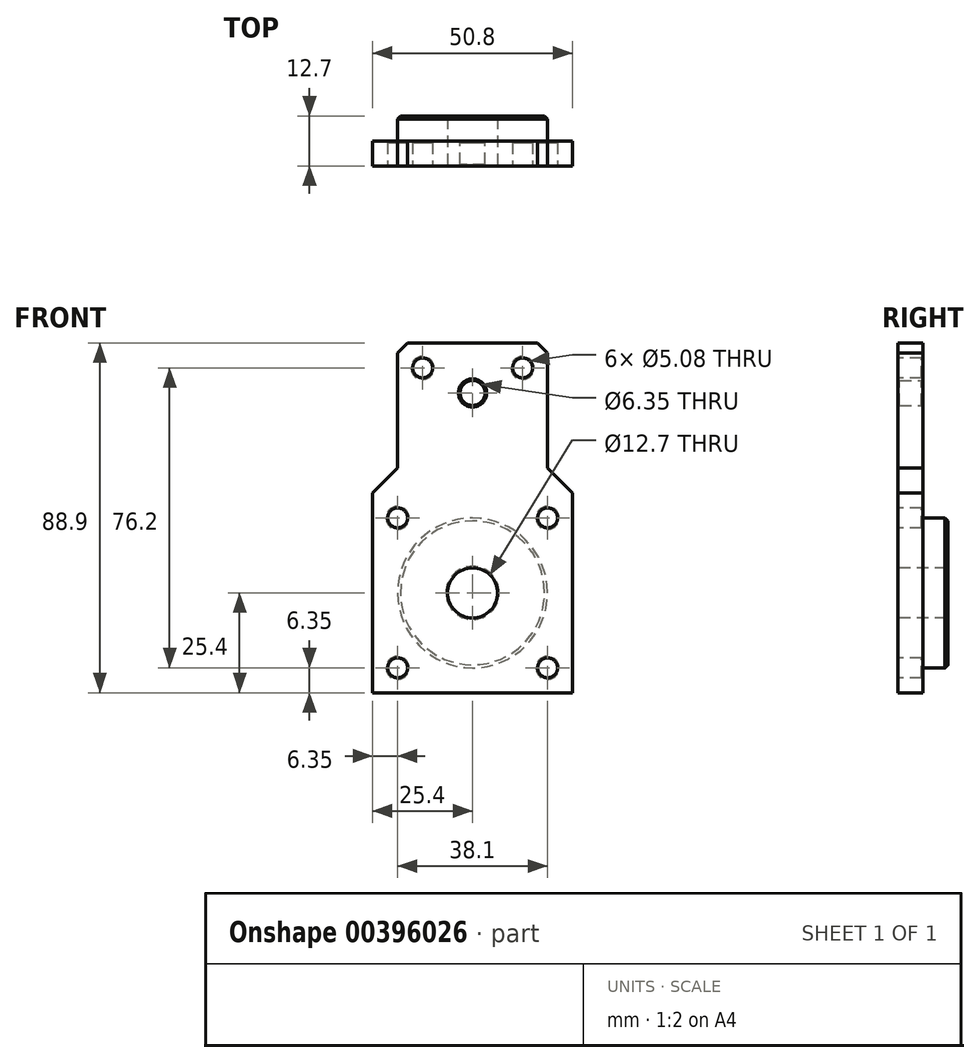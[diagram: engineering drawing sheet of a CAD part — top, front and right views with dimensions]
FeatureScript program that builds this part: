
annotation { "Feature Type Name" : "Feature", "Feature Type Description" : "" }
export const myFeature = defineFeature(function(context is Context, id is Id, definition is map)
    precondition{}
    {
        {
            var Q0;
            Q0=qCreatedBy(makeId("Front.planeOp"),FACE);
            var sketch = newSketch(context, id + "F0", { "sketchPlane" : qUnion([Q0])});
            skCircle(sketch, "E0", {"center": v(0, 0) * mm, "radius": 19.05 * mm});
            skSolve(sketch);
        }
        {
            var Q0;
            Q0 = qSketchRegion(id + "F0", true);
            extrude(context, id + "F1", {"entities" : qUnion([Q0]), "depth" : 6.35 * mm, "offsetDistance" : 25.4 * mm});
        }
        {
            var Q0;
            Q0=makeQuery(id+"F1.opExtrude","CAP_FACE",FACE,{"disambiguationData":[OSD([sQuery(id+"F0.wireOp",EDGE,"E0")])],"isStart":false});
            var sketch = newSketch(context, id + "F2", { "sketchPlane" : qUnion([Q0])});
            skLineSegment(sketch, "E1.bottom", {"start": v(-25.4, 25.4) * mm, "end": v(-19.05, 25.4) * mm});
            skLineSegment(sketch, "E1.top", {"start": v(-25.4, -25.4) * mm, "end": v(25.4, -25.4) * mm});
            skLineSegment(sketch, "E1.left", {"start": v(-25.4, 25.4) * mm, "end": v(-25.4, -25.4) * mm});
            skLineSegment(sketch, "E1.right", {"start": v(25.4, 25.4) * mm, "end": v(25.4, -25.4) * mm});
            skLineSegment(sketch, "E2", {"start": v(-19.05, 63.5) * mm, "end": v(19.05, 63.5) * mm});
            skLineSegment(sketch, "E3", {"start": v(-19.05, 63.5) * mm, "end": v(-19.05, 25.4) * mm});
            skLineSegment(sketch, "E4", {"start": v(19.05, 63.5) * mm, "end": v(19.05, 25.4) * mm});
            skLineSegment(sketch, "E5.trimOffspring", {"start": v(19.05, 25.4) * mm, "end": v(25.4, 25.4) * mm});
            skCircle(sketch, "E6", {"center": v(0, 50.8) * mm, "radius": 3.18 * mm});
            skSolve(sketch);
        }
        {
            var Q0;
            Q0 = qSketchRegion(id + "F2", true);
            extrude(context, id + "F3", {"entities" : qUnion([Q0]), "operationType" : NewBodyOperationType.ADD, "depth" : 6.35 * mm, "offsetDistance" : 25.4 * mm});
        }
        {
            var Q0;
            Q0=makeQuery(id+"F1.opExtrude","CAP_EDGE",EDGE,{"disambiguationData":[OSD([sQuery(id+"F0.wireOp",EDGE,"E0")])],"isStart":true});
            chamfer(context, id + "F4", {"entities" : qUnion([Q0]), "width" : 0.76 * mm, "tangentPropagation" : true});
        }
        {
            var Q0;
            Q0=makeQuery(id+"F3.opExtrude","CAP_FACE",FACE,{"disambiguationData":[OSD([sQuery(id+"F2.wireOp",EDGE,"E1.bottom"),sQuery(id+"F2.wireOp",EDGE,"E1.top"),sQuery(id+"F2.wireOp",EDGE,"E1.left"),sQuery(id+"F2.wireOp",EDGE,"E1.right")])],"isStart":false});
            var sketch = newSketch(context, id + "F5", { "sketchPlane" : qUnion([Q0])});
            skCircle(sketch, "E7", {"center": v(0, 0) * mm, "radius": 6.35 * mm});
            skCircle(sketch, "E8.cCircle", {"center": v(0, 0) * mm, "radius": 19.05 * mm, "construction": true});
            skPoint(sketch, "E8.0.midPoint", {"position": v(0, 19.05) * mm});
            skCircle(sketch, "E9", {"center": v(-19.05, 19.05) * mm, "radius": 2.54 * mm});
            skCircle(sketch, "E10", {"center": v(19.05, 19.05) * mm, "radius": 2.54 * mm});
            skCircle(sketch, "E11", {"center": v(19.05, -19.05) * mm, "radius": 2.54 * mm});
            skCircle(sketch, "E12", {"center": v(-19.05, -19.05) * mm, "radius": 2.54 * mm});
            skCircle(sketch, "E13", {"center": v(-12.7, 57.15) * mm, "radius": 2.54 * mm});
            skCircle(sketch, "E14", {"center": v(12.7, 57.15) * mm, "radius": 2.54 * mm});
            skSolve(sketch);
        }
        {
            var Q0;
            Q0 = qSketchRegion(id + "F5", true);
            extrude(context, id + "F6", {"entities" : qUnion([Q0]), "operationType" : NewBodyOperationType.REMOVE, "oppositeDirection" : true, "depth" : 12.7 * mm, "offsetDistance" : 25.4 * mm});
        }
        {
            var Q0;
            Q0=makeQuery(id+"F6.boolean.opBoolean","COPY",EDGE,{"derivedFrom":makeQuery(id+"F6.opExtrude","CAP_EDGE",EDGE,{"disambiguationData":[OSD([sQuery(id+"F5.wireOp",EDGE,"E9")])],"isStart":true})});
            var Q1;
            Q1=makeQuery(id+"F6.boolean.opBoolean","COPY",EDGE,{"derivedFrom":makeQuery(id+"F6.opExtrude","CAP_EDGE",EDGE,{"disambiguationData":[OSD([sQuery(id+"F5.wireOp",EDGE,"E10")])],"isStart":true})});
            var Q2;
            Q2=makeQuery(id+"F6.boolean.opBoolean","COPY",EDGE,{"derivedFrom":makeQuery(id+"F6.opExtrude","CAP_EDGE",EDGE,{"disambiguationData":[OSD([sQuery(id+"F5.wireOp",EDGE,"E11")])],"isStart":true})});
            var Q3;
            Q3=makeQuery(id+"F6.boolean.opBoolean","COPY",EDGE,{"derivedFrom":makeQuery(id+"F6.opExtrude","CAP_EDGE",EDGE,{"disambiguationData":[OSD([sQuery(id+"F5.wireOp",EDGE,"E12")])],"isStart":true})});
            var Q4;
            Q4=makeQuery(id+"F6.boolean.opBoolean","COPY",EDGE,{"derivedFrom":makeQuery(id+"F6.opExtrude","CAP_EDGE",EDGE,{"disambiguationData":[OSD([sQuery(id+"F5.wireOp",EDGE,"E7")])],"isStart":true})});
            var Q5;
            Q5=makeQuery(id+"F6.boolean.opBoolean","INTERSECT",EDGE,{"derivedFrom":[makeQuery(id+"F1.opExtrude","CAP_FACE",FACE,{"disambiguationData":[OSD([sQuery(id+"F0.wireOp",EDGE,"E0")])],"isStart":true}),makeQuery(id+"F6.opExtrude","SWEPT_FACE",FACE,{"disambiguationData":[OSD([sQuery(id+"F5.wireOp",EDGE,"E7")])]})]});
            var Q6;
            Q6=makeQuery(id+"F6.boolean.opBoolean","COPY",EDGE,{"derivedFrom":makeQuery(id+"F6.opExtrude","CAP_EDGE",EDGE,{"disambiguationData":[OSD([sQuery(id+"F5.wireOp",EDGE,"E7")])],"isStart":false})});
            var Q7;
            Q7=makeQuery(id+"F6.boolean.opBoolean","INTERSECT",EDGE,{"derivedFrom":[makeQuery(id+"F3.opExtrude","CAP_FACE",FACE,{"disambiguationData":[OSD([sQuery(id+"F2.wireOp",EDGE,"E1.bottom"),sQuery(id+"F2.wireOp",EDGE,"E1.top"),sQuery(id+"F2.wireOp",EDGE,"E1.left"),sQuery(id+"F2.wireOp",EDGE,"E1.right")])],"isStart":true}),makeQuery(id+"F6.opExtrude","SWEPT_FACE",FACE,{"disambiguationData":[OSD([sQuery(id+"F5.wireOp",EDGE,"E11")])]})]});
            var Q8;
            Q8=makeQuery(id+"F6.boolean.opBoolean","INTERSECT",EDGE,{"derivedFrom":[makeQuery(id+"F3.opExtrude","CAP_FACE",FACE,{"disambiguationData":[OSD([sQuery(id+"F2.wireOp",EDGE,"E1.bottom"),sQuery(id+"F2.wireOp",EDGE,"E1.top"),sQuery(id+"F2.wireOp",EDGE,"E1.left"),sQuery(id+"F2.wireOp",EDGE,"E1.right")])],"isStart":true}),makeQuery(id+"F6.opExtrude","SWEPT_FACE",FACE,{"disambiguationData":[OSD([sQuery(id+"F5.wireOp",EDGE,"E12")])]})]});
            var Q9;
            Q9=makeQuery(id+"F6.boolean.opBoolean","INTERSECT",EDGE,{"derivedFrom":[makeQuery(id+"F3.opExtrude","CAP_FACE",FACE,{"disambiguationData":[OSD([sQuery(id+"F2.wireOp",EDGE,"E1.bottom"),sQuery(id+"F2.wireOp",EDGE,"E1.top"),sQuery(id+"F2.wireOp",EDGE,"E1.left"),sQuery(id+"F2.wireOp",EDGE,"E1.right")])],"isStart":true}),makeQuery(id+"F6.opExtrude","SWEPT_FACE",FACE,{"disambiguationData":[OSD([sQuery(id+"F5.wireOp",EDGE,"E9")])]})]});
            var Q10;
            Q10=makeQuery(id+"F6.boolean.opBoolean","INTERSECT",EDGE,{"derivedFrom":[makeQuery(id+"F3.opExtrude","CAP_FACE",FACE,{"disambiguationData":[OSD([sQuery(id+"F2.wireOp",EDGE,"E1.bottom"),sQuery(id+"F2.wireOp",EDGE,"E1.top"),sQuery(id+"F2.wireOp",EDGE,"E1.left"),sQuery(id+"F2.wireOp",EDGE,"E1.right")])],"isStart":true}),makeQuery(id+"F6.opExtrude","SWEPT_FACE",FACE,{"disambiguationData":[OSD([sQuery(id+"F5.wireOp",EDGE,"E10")])]})]});
            var Q11;
            Q11=makeQuery(id+"F6.boolean.opBoolean","COPY",EDGE,{"derivedFrom":makeQuery(id+"F6.opExtrude","CAP_EDGE",EDGE,{"disambiguationData":[OSD([sQuery(id+"F5.wireOp",EDGE,"E13")])],"isStart":true})});
            var Q12;
            Q12=makeQuery(id+"F6.boolean.opBoolean","COPY",EDGE,{"derivedFrom":makeQuery(id+"F6.opExtrude","CAP_EDGE",EDGE,{"disambiguationData":[OSD([sQuery(id+"F5.wireOp",EDGE,"E14")])],"isStart":true})});
            var Q13;
            Q13=makeQuery(id+"F6.boolean.opBoolean","INTERSECT",EDGE,{"derivedFrom":[makeQuery(id+"F3.opExtrude","CAP_FACE",FACE,{"disambiguationData":[OSD([sQuery(id+"F2.wireOp",EDGE,"E1.bottom"),sQuery(id+"F2.wireOp",EDGE,"E1.top"),sQuery(id+"F2.wireOp",EDGE,"E1.left"),sQuery(id+"F2.wireOp",EDGE,"E1.right"),sQuery(id+"F2.wireOp",EDGE,"E2"),sQuery(id+"F2.wireOp",EDGE,"E3"),sQuery(id+"F2.wireOp",EDGE,"E4"),sQuery(id+"F2.wireOp",EDGE,"E5.trimOffspring"),sQuery(id+"F2.wireOp",EDGE,"E6")])],"isStart":true}),makeQuery(id+"F6.opExtrude","SWEPT_FACE",FACE,{"disambiguationData":[OSD([sQuery(id+"F5.wireOp",EDGE,"E13")])]})]});
            var Q14;
            Q14=makeQuery(id+"F6.boolean.opBoolean","INTERSECT",EDGE,{"derivedFrom":[makeQuery(id+"F3.opExtrude","CAP_FACE",FACE,{"disambiguationData":[OSD([sQuery(id+"F2.wireOp",EDGE,"E1.bottom"),sQuery(id+"F2.wireOp",EDGE,"E1.top"),sQuery(id+"F2.wireOp",EDGE,"E1.left"),sQuery(id+"F2.wireOp",EDGE,"E1.right"),sQuery(id+"F2.wireOp",EDGE,"E2"),sQuery(id+"F2.wireOp",EDGE,"E3"),sQuery(id+"F2.wireOp",EDGE,"E4"),sQuery(id+"F2.wireOp",EDGE,"E5.trimOffspring"),sQuery(id+"F2.wireOp",EDGE,"E6")])],"isStart":true}),makeQuery(id+"F6.opExtrude","SWEPT_FACE",FACE,{"disambiguationData":[OSD([sQuery(id+"F5.wireOp",EDGE,"E14")])]})]});
            var Q15;
            Q15=makeQuery(id+"F3.opExtrude","CAP_EDGE",EDGE,{"disambiguationData":[OSD([sQuery(id+"F2.wireOp",EDGE,"E6")])],"isStart":true});
            var Q16;
            Q16=makeQuery(id+"F3.opExtrude","CAP_EDGE",EDGE,{"disambiguationData":[OSD([sQuery(id+"F2.wireOp",EDGE,"E6")])],"isStart":false});
            chamfer(context, id + "F7", {"entities" : qUnion([Q0, Q1, Q2, Q3, Q4, Q5, Q6, Q7, Q8, Q9, Q10, Q11, Q12, Q13, Q14, Q15, Q16]), "width" : 0.38 * mm, "tangentPropagation" : true});
        }
        {
            var Q0;
            Q0=makeQuery(id+"F3.opExtrude","SWEPT_EDGE",EDGE,{"disambiguationData":[OSD([sQuery(id+"F2.wireOp",EDGE,"E1.bottom"),sQuery(id+"F2.wireOp",EDGE,"E3")])]});
            var Q1;
            Q1=makeQuery(id+"F3.opExtrude","SWEPT_EDGE",EDGE,{"disambiguationData":[OSD([sQuery(id+"F2.wireOp",EDGE,"E4"),sQuery(id+"F2.wireOp",EDGE,"E5.trimOffspring")])]});
            chamfer(context, id + "F8", {"entities" : qUnion([Q0, Q1]), "width" : 6.35 * mm, "tangentPropagation" : true});
        }
        {
            var Q0;
            Q0=makeQuery(id+"F3.opExtrude","SWEPT_EDGE",EDGE,{"disambiguationData":[OSD([sQuery(id+"F2.wireOp",EDGE,"E2"),sQuery(id+"F2.wireOp",EDGE,"E3")])]});
            var Q1;
            Q1=makeQuery(id+"F3.opExtrude","SWEPT_EDGE",EDGE,{"disambiguationData":[OSD([sQuery(id+"F2.wireOp",EDGE,"E2"),sQuery(id+"F2.wireOp",EDGE,"E4")])]});
            chamfer(context, id + "F9", {"entities" : qUnion([Q0, Q1]), "width" : 2.54 * mm, "tangentPropagation" : true});
        }
    });
